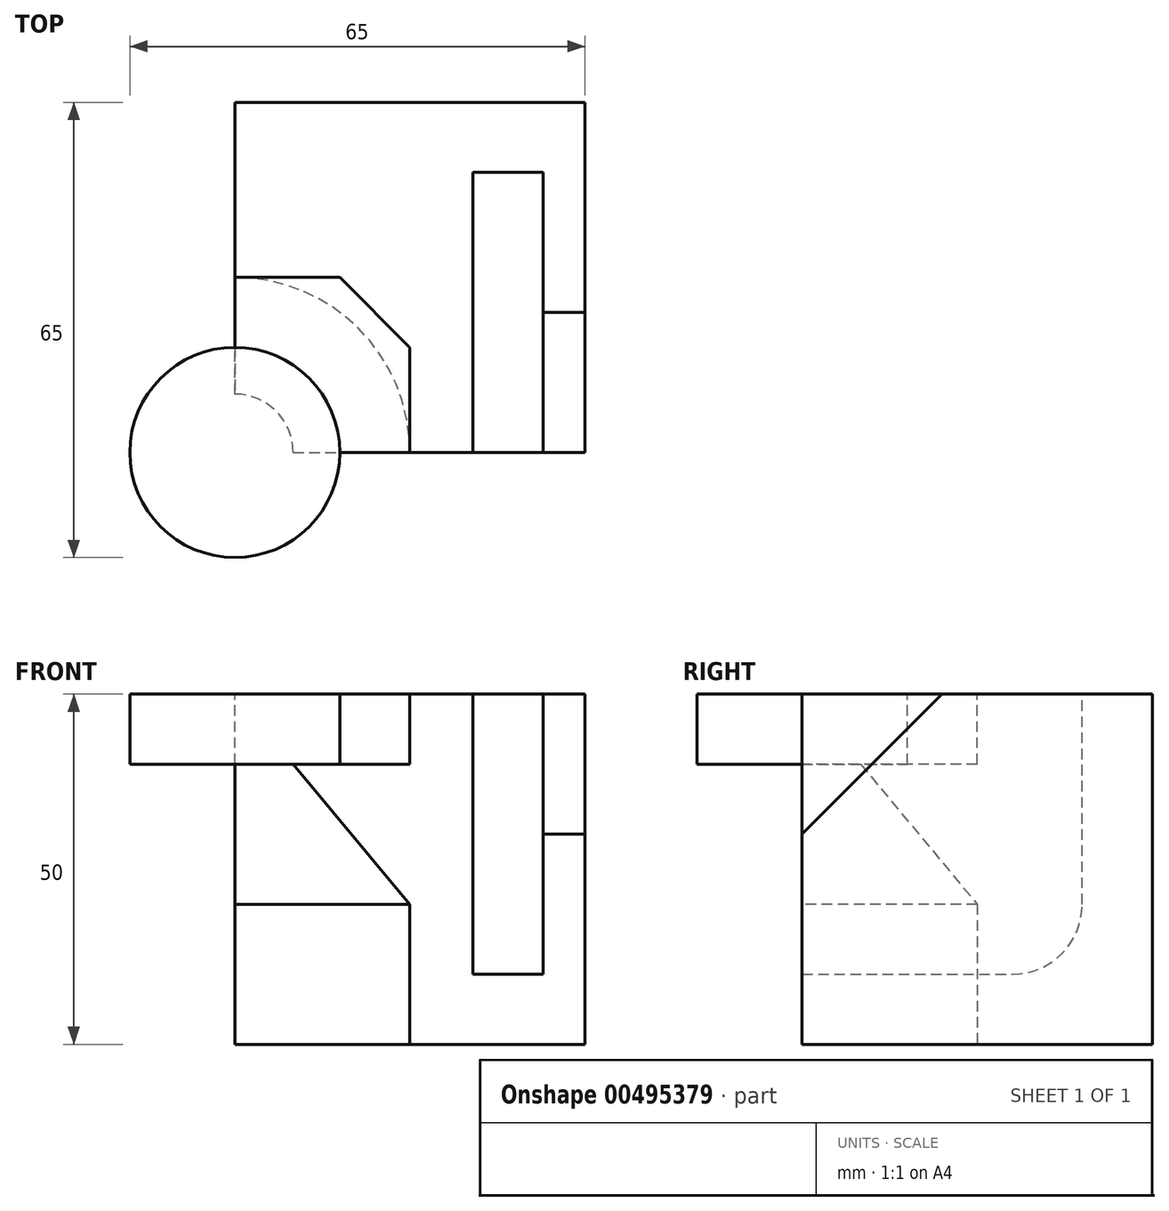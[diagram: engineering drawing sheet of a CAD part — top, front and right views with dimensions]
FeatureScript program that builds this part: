
annotation { "Feature Type Name" : "Feature", "Feature Type Description" : "" }
export const myFeature = defineFeature(function(context is Context, id is Id, definition is map)
    precondition{}
    {
        {
            var Q0;
            Q0=qCreatedBy(makeId("Right.planeOp"),FACE);
            var sketch = newSketch(context, id + "F0", { "sketchPlane" : qUnion([Q0])});
            skLineSegment(sketch, "E0.bottom", {"start": v(0, 0) * mm, "end": v(-50, 0) * mm});
            skLineSegment(sketch, "E0.top", {"start": v(0, 50) * mm, "end": v(-50, 50) * mm});
            skLineSegment(sketch, "E0.left", {"start": v(0, 0) * mm, "end": v(0, 50) * mm});
            skLineSegment(sketch, "E0.right", {"start": v(-50, 0) * mm, "end": v(-50, 50) * mm});
            skLineSegment(sketch, "E1", {"start": v(-50, 50) * mm, "end": v(-50, 30) * mm});
            skLineSegment(sketch, "E2", {"start": v(-50, 30) * mm, "end": v(-30, 50) * mm});
            skLineSegment(sketch, "E3", {"start": v(-30, 50) * mm, "end": v(-50, 50) * mm});
            skSolve(sketch);
        }
        {
            var Q0;
            Q0=makeQuery(id+"F0.imprint","IMPRINT",FACE,{"disambiguationData":[TD([[makeQuery(id+"F0.imprint","IMPRINT",EDGE,{"derivedFrom":sQuery(id+"F0.wireOp",EDGE,"E0.bottom")}),-1.0]])]});
            extrude(context, id + "F1", {"entities" : qUnion([Q0]), "oppositeDirection" : true, "depth" : 6 * mm});
        }
        {
            var Q0;
            Q0=makeQuery(id+"F1.opExtrude","CAP_FACE",FACE,{"disambiguationData":[OSD([sQuery(id+"F0.wireOp",EDGE,"E0.bottom"),sQuery(id+"F0.wireOp",EDGE,"E0.top"),sQuery(id+"F0.wireOp",EDGE,"E0.left"),sQuery(id+"F0.wireOp",EDGE,"E0.right"),sQuery(id+"F0.wireOp",EDGE,"E2")])],"isStart":false});
            var sketch = newSketch(context, id + "F2", { "sketchPlane" : qUnion([Q0])});
            skLineSegment(sketch, "E4", {"start": v(50, 0) * mm, "end": v(50, 10) * mm});
            skLineSegment(sketch, "E5", {"start": v(50, 10) * mm, "end": v(20, 10) * mm});
            skLineSegment(sketch, "E6", {"start": v(10, 20) * mm, "end": v(10, 50) * mm});
            skLineSegment(sketch, "E7", {"start": v(10, 50) * mm, "end": v(0, 50) * mm});
            skPoint(sketch, "E8.visualSharp", {"position": v(10, 10) * mm});
            skArc(sketch, "E8.filletArc", {"start": v(10, 20) * mm, "mid": v(12.93, 12.93) * mm, "end": v(20, 10) * mm});
            skSolve(sketch);
        }
        {
            var Q0;
            Q0 = qSketchRegion(id + "F2", true);
            var Q1;
            Q1=makeQuery(id+"F2.imprint","IMPRINT",FACE,{"disambiguationData":[TD([[makeQuery(id+"F2.imprint","IMPRINT",EDGE,{"derivedFrom":sQuery(id+"F2.wireOp",EDGE,"E4")}),1.0]])]});
            extrude(context, id + "F3", {"entities" : qUnion([Q0, Q1]), "operationType" : NewBodyOperationType.ADD, "depth" : 10 * mm});
        }
        {
            var Q0;
            Q0=makeQuery(id+"F3.opExtrude","CAP_FACE",FACE,{"disambiguationData":[OSD([sQuery(id+"F0.wireOp",EDGE,"E0.bottom"),sQuery(id+"F0.wireOp",EDGE,"E0.left"),sQuery(id+"F2.wireOp",EDGE,"E4"),sQuery(id+"F2.wireOp",EDGE,"E5"),sQuery(id+"F2.wireOp",EDGE,"E6"),sQuery(id+"F2.wireOp",EDGE,"E7"),sQuery(id+"F2.wireOp",EDGE,"E8.filletArc")])],"isStart":false});
            var sketch = newSketch(context, id + "F4", { "sketchPlane" : qUnion([Q0])});
            skLineSegment(sketch, "E9.bottom", {"start": v(0, 0) * mm, "end": v(50, 0) * mm});
            skLineSegment(sketch, "E9.top", {"start": v(0, 50) * mm, "end": v(50, 50) * mm});
            skLineSegment(sketch, "E9.left", {"start": v(0, 0) * mm, "end": v(0, 50) * mm});
            skLineSegment(sketch, "E9.right", {"start": v(50, 0) * mm, "end": v(50, 50) * mm});
            skSolve(sketch);
        }
        {
            var Q0;
            Q0 = qSketchRegion(id + "F4", true);
            extrude(context, id + "F5", {"entities" : qUnion([Q0]), "operationType" : NewBodyOperationType.ADD, "depth" : 34 * mm});
        }
        {
            var Q0;
            Q0=makeQuery(id+"F5.boolean.opBoolean","MERGE",FACE,{"derivedFrom":[makeQuery(id+"F3.boolean.opBoolean","MERGE",FACE,{"derivedFrom":[makeQuery(id+"F1.opExtrude","SWEPT_FACE",FACE,{"disambiguationData":[OSD([sQuery(id+"F0.wireOp",EDGE,"E0.top")])]}),makeQuery(id+"F3.opExtrude","SWEPT_FACE",FACE,{"disambiguationData":[OSD([sQuery(id+"F2.wireOp",EDGE,"E7")])]})]}),makeQuery(id+"F5.opExtrude","SWEPT_FACE",FACE,{"disambiguationData":[OSD([sQuery(id+"F4.wireOp",EDGE,"E9.top")])]})]});
            var sketch = newSketch(context, id + "F6", { "sketchPlane" : qUnion([Q0])});
            skLineSegment(sketch, "E10.bottom", {"start": v(-50, -50) * mm, "end": v(-25, -50) * mm});
            skLineSegment(sketch, "E10.top", {"start": v(-50, -25) * mm, "end": v(-25, -25) * mm});
            skLineSegment(sketch, "E10.left", {"start": v(-50, -50) * mm, "end": v(-50, -25) * mm});
            skLineSegment(sketch, "E10.right", {"start": v(-25, -50) * mm, "end": v(-25, -25) * mm});
            skLineSegment(sketch, "E11", {"start": v(-25, -25) * mm, "end": v(-35, -25) * mm});
            skLineSegment(sketch, "E12", {"start": v(-35, -25) * mm, "end": v(-25, -35) * mm});
            skLineSegment(sketch, "E13", {"start": v(-25, -35) * mm, "end": v(-25, -25) * mm});
            skSolve(sketch);
        }
        {
            var Q0;
            Q0=makeQuery(id+"F6.imprint","IMPRINT",FACE,{"disambiguationData":[TD([[makeQuery(id+"F6.imprint","IMPRINT",EDGE,{"derivedFrom":sQuery(id+"F6.wireOp",EDGE,"E10.bottom")}),1.0]])]});
            extrude(context, id + "F7", {"entities" : qUnion([Q0]), "operationType" : NewBodyOperationType.REMOVE, "oppositeDirection" : true, "depth" : 10 * mm});
        }
        {
            var Q0;
            Q0=makeQuery(id+"F7.boolean.opBoolean","COPY",FACE,{"derivedFrom":makeQuery(id+"F7.opExtrude","CAP_FACE",FACE,{"disambiguationData":[OSD([sQuery(id+"F6.wireOp",EDGE,"E10.bottom"),sQuery(id+"F6.wireOp",EDGE,"E10.top"),sQuery(id+"F6.wireOp",EDGE,"E10.left"),sQuery(id+"F6.wireOp",EDGE,"E10.right"),sQuery(id+"F6.wireOp",EDGE,"E12")])],"isStart":false})});
            var sketch = newSketch(context, id + "F8", { "sketchPlane" : qUnion([Q0])});
            skCircle(sketch, "E14", {"center": v(-50, -50) * mm, "radius": 15 * mm});
            skSolve(sketch);
        }
        {
            var Q0;
            {var subQ0=sQuery(id+"F8.wireOp",EDGE,"E14");var subQ1=makeQuery(id+"F7.boolean.opBoolean","COPY",EDGE,{"derivedFrom":makeQuery(id+"F7.opExtrude","CAP_EDGE",EDGE,{"disambiguationData":[OSD([sQuery(id+"F6.wireOp",EDGE,"E10.bottom")])],"isStart":false})});var subQ2=makeQuery(id+"F8.imprint","INTERSECT",VERTEX,{"derivedFrom":[subQ1,subQ0]});Q0=makeQuery(id+"F8.imprint","IMPRINT",FACE,{"disambiguationData":[TD([[makeQuery(id+"F8.imprint","IMPRINT",EDGE,{"disambiguationData":[TD([[subQ2,-1.0]])],"derivedFrom":subQ0}),1.0]])]});}
            extrude(context, id + "F9", {"entities" : qUnion([Q0]), "operationType" : NewBodyOperationType.ADD, "depth" : 10 * mm});
        }
        {
            var Q0;
            {var subQ0=sQuery(id+"F0.wireOp",EDGE,"E0.bottom");Q0=makeQuery(id+"F5.boolean.opBoolean","MERGE",FACE,{"derivedFrom":[makeQuery(id+"F3.boolean.opBoolean","MERGE",FACE,{"derivedFrom":[makeQuery(id+"F1.opExtrude","SWEPT_FACE",FACE,{"disambiguationData":[OSD([subQ0])]}),makeQuery(id+"F3.opExtrude","SWEPT_FACE",FACE,{"disambiguationData":[OSD([subQ0])]})]}),makeQuery(id+"F5.opExtrude","SWEPT_FACE",FACE,{"disambiguationData":[OSD([sQuery(id+"F4.wireOp",EDGE,"E9.bottom")])]})]});}
            var sketch = newSketch(context, id + "F10", { "sketchPlane" : qUnion([Q0])});
            skCircle(sketch, "E15", {"center": v(-50, 50) * mm, "radius": 25 * mm});
            skSolve(sketch);
        }
        {
            var Q0;
            {var subQ0=sQuery(id+"F10.wireOp",EDGE,"E15");var subQ1=sQuery(id+"F4.wireOp",EDGE,"E9.bottom");var subQ2=makeQuery(id+"F5.opExtrude","CAP_EDGE",EDGE,{"disambiguationData":[OSD([subQ1])],"isStart":false});var subQ3=makeQuery(id+"F10.imprint","INTERSECT",VERTEX,{"derivedFrom":[subQ2,subQ0]});Q0=makeQuery(id+"F10.imprint","IMPRINT",FACE,{"disambiguationData":[TD([[makeQuery(id+"F10.imprint","IMPRINT",EDGE,{"disambiguationData":[TD([[subQ3,-1.0]])],"derivedFrom":subQ0}),1.0]])]});}
            extrude(context, id + "F11", {"entities" : qUnion([Q0]), "operationType" : NewBodyOperationType.REMOVE, "oppositeDirection" : true, "depth" : 20 * mm});
        }
        {
            var Q0;
            Q0=makeQuery(id+"F9.boolean.opBoolean","MERGE",FACE,{"derivedFrom":[makeQuery(id+"F5.boolean.opBoolean","MERGE",FACE,{"derivedFrom":[makeQuery(id+"F3.boolean.opBoolean","MERGE",FACE,{"derivedFrom":[makeQuery(id+"F1.opExtrude","SWEPT_FACE",FACE,{"disambiguationData":[OSD([sQuery(id+"F0.wireOp",EDGE,"E0.right")])]}),makeQuery(id+"F3.opExtrude","SWEPT_FACE",FACE,{"disambiguationData":[OSD([sQuery(id+"F2.wireOp",EDGE,"E4")])]})]}),makeQuery(id+"F5.opExtrude","SWEPT_FACE",FACE,{"disambiguationData":[OSD([sQuery(id+"F4.wireOp",EDGE,"E9.right")])]})]}),makeQuery(id+"F9.opExtrude","SWEPT_FACE",FACE,{"disambiguationData":[OSD([sQuery(id+"F6.wireOp",EDGE,"E10.bottom")])]})]});
            var sketch = newSketch(context, id + "F12", { "sketchPlane" : qUnion([Q0])});
            skLineSegment(sketch, "E16", {"start": v(-50, 50) * mm, "end": v(-25, 20) * mm});
            skSolve(sketch);
        }
        {
            var Q0;
            Q0=makeQuery(id+"F9.boolean.opBoolean","MERGE",FACE,{"derivedFrom":[makeQuery(id+"F5.opExtrude","CAP_FACE",FACE,{"disambiguationData":[OSD([sQuery(id+"F4.wireOp",EDGE,"E9.bottom"),sQuery(id+"F4.wireOp",EDGE,"E9.top"),sQuery(id+"F4.wireOp",EDGE,"E9.left"),sQuery(id+"F4.wireOp",EDGE,"E9.right")])],"isStart":false}),makeQuery(id+"F9.opExtrude","SWEPT_FACE",FACE,{"disambiguationData":[OSD([sQuery(id+"F6.wireOp",EDGE,"E10.left")])]})]});
            var sketch = newSketch(context, id + "F13", { "sketchPlane" : qUnion([Q0])});
            skLineSegment(sketch, "E17", {"start": v(50, 50) * mm, "end": v(25, 20) * mm});
            skSolve(sketch);
        }
        {
            var Q0;
            Q0=makeQuery(id+"F12.imprint","IMPRINT",FACE,{"disambiguationData":[TD([[makeQuery(id+"F12.imprint","IMPRINT",EDGE,{"derivedFrom":sQuery(id+"F12.wireOp",EDGE,"E16")}),-1.0]])]});
            var Q1;
            Q1=makeQuery(id+"F13.imprint","IMPRINT",FACE,{"disambiguationData":[TD([[makeQuery(id+"F13.imprint","IMPRINT",EDGE,{"derivedFrom":sQuery(id+"F13.wireOp",EDGE,"E17")}),1.0]])]});
            var Q2;
            Q2=makeQuery(id+"F11.boolean.opBoolean","COPY",EDGE,{"derivedFrom":makeQuery(id+"F11.opExtrude","CAP_EDGE",EDGE,{"disambiguationData":[OSD([sQuery(id+"F10.wireOp",EDGE,"E15")])],"isStart":false})});
            sweep(context, id + "F14", {"operationType" : NewBodyOperationType.REMOVE, "profiles" : qUnion([Q0, Q1]), "path" : qUnion([Q2])});
        }
    });
